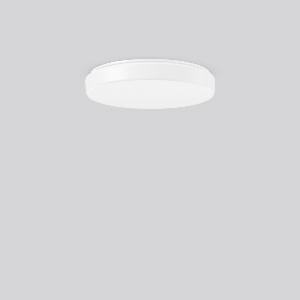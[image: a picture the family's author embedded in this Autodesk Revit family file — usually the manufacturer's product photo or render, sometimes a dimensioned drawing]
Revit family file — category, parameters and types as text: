
# Revit family: flat_polymero_kreis_slim_312085_002_1_8428
name_source: partatom
category: Lighting Fixtures
units: mm (PartAtom-declared; Revit-internal decimal feet)

## family parameters
Cut with Voids When Loaded = No
Host = Face
Light Source = No
Part Type = Normal
Room Calculation Point = No
Round Connector Dimension = Use Diameter
Shared = No

## types (1)
- FLAT POLYMERO KREIS SLIM (1 x LED Modul 830, 1900 lm, 3000)
    Apparent Load = 19 VA
    CIE Flux Codes = 42 73 92 85 100
    Color Rendering = 80
    Color Temperature = 3000
    Default Elevation = 1800 mm
    Description = Series: FLAT POLYMERO KREIS SLIM
Flat decorative round LED surface-mounted luminaire. Base: metal, powder-coated. Diffuser made of non-yellowing plastic (PMMA), opal. Diffuser fastening: patented push system. Suitable for Ceiling mounting, Wall (surface). 
Colour: white
Diameter: 360 mm
Height: 65 mm
Lamp: LED
Socket: without socket
Colour temperature: 3000K
Colour rendering index (CRI): 80
System power: 19 W
Rated luminous flux: 1900 lm
Luminous efficiency: 100 lm/W
Control gear: AC Strom, dim.Ph.an-/abschnitt
Protection class: I
Type of protection: IP 40
    Height = 65 mm
    Lamp = 1 x LED Modul 830
    Lamp Light Flux = 1900 lm
    Lamp count = 1
    Length = 360 mm
    Lifetime = 50000 h
    Luminous efficacy = 100 lm/W
    Manufacturer = RZB
    ModVariant = No
    Model = 312085.002.1
    Mounting Place = Ceiling, Wall
    Mounting Type = Surface mounted
    Number of Poles = 1
    OnlyDefault = Yes
    Power Factor = 1
    Product Name = FLAT POLYMERO KREIS SLIM
    Product group = Surface mounted ceiling and wall luminaires
    ProductGroupID = 305
    Protection Class = Protection class I
    Protection Degree = IP 40
    RLX_Detail_Level = 1
    RLX_Emergency_Light_Flux = 0 lm
    RLX_Emergency_Type = 0
    RLX_Emergency_Type_DB = No
    RlxData = <blob elided: 55861 chars, md5=4d84d514>
    Socket = socket
    Standby Power = 0 W
    System Light Flux = 1900 lm
    System Power = 19 W
    Type Comments = Product without accessories
    Type Image = 312085.002.jpg
    URL = http://relux.com
    VarID = ---
    Voltage = 230 V
    Voltage Range = 220-240 V
    Weight = 0.00 kg
    Width = 0 mm  [stored 0 ft]

note: [stored X ft] marks values corroborated as IEEE doubles in the binary element streams (Revit-internal decimal feet)

## geometry (parser evidence)
native form markers: Blend x4, Sweep x12
no freeform markers — native parametric forms only
